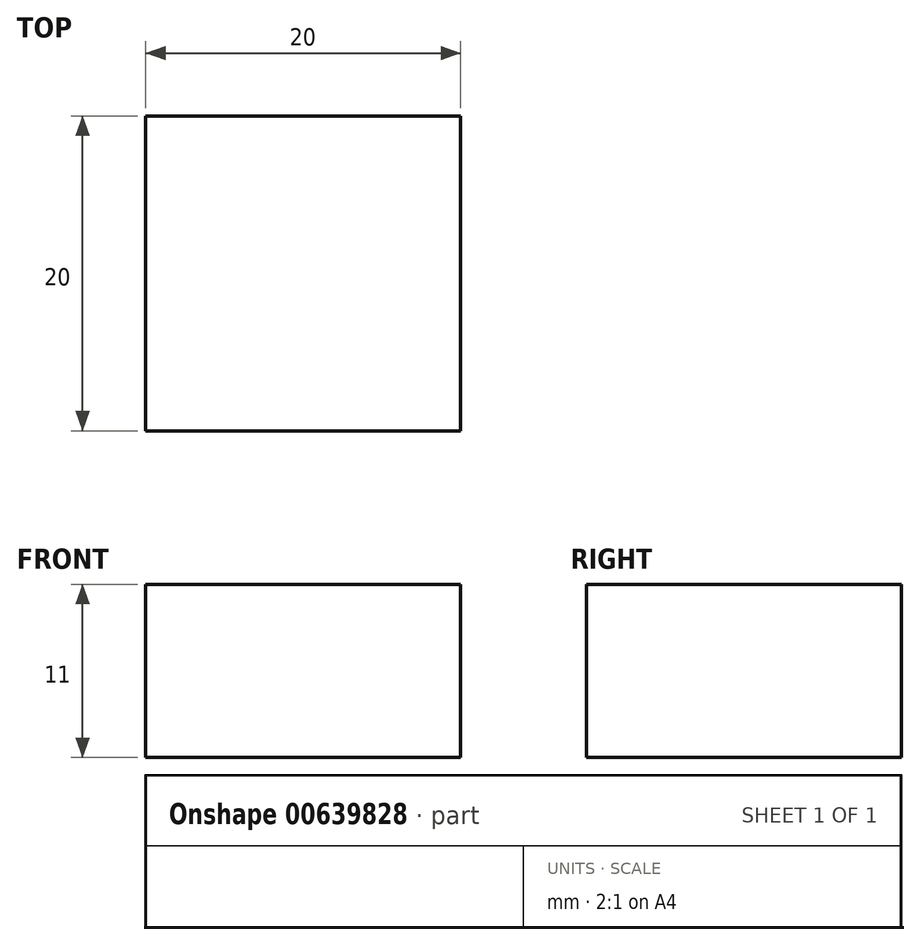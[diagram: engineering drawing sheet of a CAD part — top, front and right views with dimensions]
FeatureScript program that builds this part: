
annotation { "Feature Type Name" : "Feature", "Feature Type Description" : "" }
export const myFeature = defineFeature(function(context is Context, id is Id, definition is map)
    precondition{}
    {
        {
            var Q0;
            Q0=qCreatedBy(makeId("Top.planeOp"),FACE);
            var sketch = newSketch(context, id + "F0", { "sketchPlane" : qUnion([Q0])});
            skLineSegment(sketch, "E0.bottom", {"start": v(10, -10) * mm, "end": v(-10, -10) * mm});
            skLineSegment(sketch, "E0.top", {"start": v(10, 10) * mm, "end": v(-10, 10) * mm});
            skLineSegment(sketch, "E0.left", {"start": v(10, -10) * mm, "end": v(10, 10) * mm});
            skLineSegment(sketch, "E0.right", {"start": v(-10, -10) * mm, "end": v(-10, 10) * mm});
            skPoint(sketch, "E0.middle", {"position": v(0, 0) * mm});
            skSolve(sketch);
        }
        {
            var Q0;
            Q0=makeQuery(id+"F0.imprint","IMPRINT",FACE,{"disambiguationData":[TD([[makeQuery(id+"F0.imprint","IMPRINT",EDGE,{"derivedFrom":sQuery(id+"F0.wireOp",EDGE,"E0.bottom")}),-1.0]])]});
            extrude(context, id + "F1", {"entities" : qUnion([Q0]), "depth" : 11 * mm, "offsetDistance" : 25 * mm});
        }
    });
